# Revit family: Fam Bticino door entry system IP outdoor unit
name_source: partatom
category: Tableaux/Baies
units: mm (PartAtom-declared; Revit-internal decimal feet)

## family parameters
Configuration du panneau = Deux colonnes, circuits au sein
Conserver l'orientation des annotations = Non
Cote de connecteur circulaire = Utiliser le diamètre
Couper avec des vides une fois chargée = Non
Hôte = Face
Partagée = Non
Repère de localisation dans la pièce = Non
Type d'élément = Tableau de raccordement

## types (1)
- IP type outdoor black 24V
    Color = Black
    EAN = 8005543732304
    Elévation par défaut = 1500 mm
    Etim class = LC001351 Push button panel door communication
    Fabricant = BTICINO
    General terms of use = https://assets.legrand.com
    Height = 161 mm
    IK = 07
    IP = 54
    Installation method = Surface
    Interface type = Wire network
    Operating temperature min max = -10/+50 °C
    Photo = https://assets.legrand.com
    Product designation = BTicino door entry system IP outdoor unit BT-374006
    Reference = BT-374006
    Tension = 24 V DC
    Touch screen = Non
    Width = 100 mm  [stored 0.328084 ft]
    With camera = Oui

note: [stored X ft] marks values corroborated as IEEE doubles in the binary element streams (Revit-internal decimal feet)
